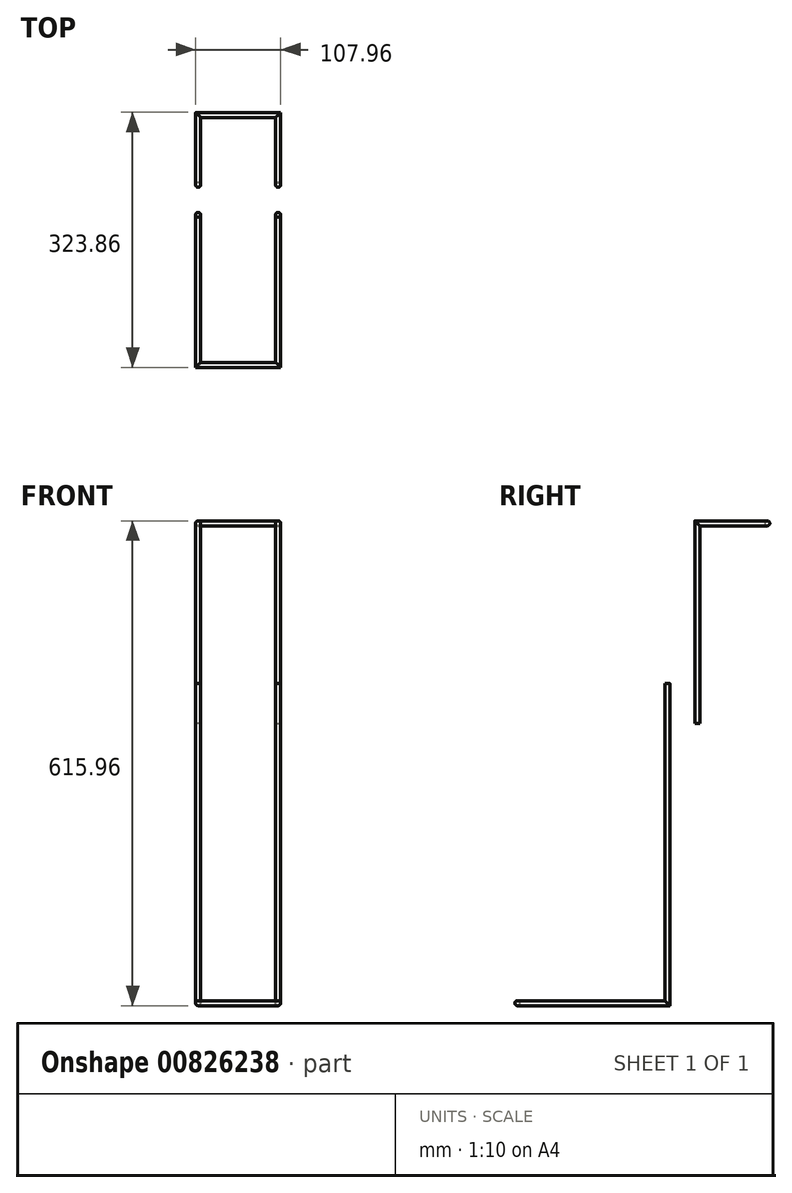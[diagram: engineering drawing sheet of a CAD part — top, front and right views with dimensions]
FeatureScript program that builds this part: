
annotation { "Feature Type Name" : "Feature", "Feature Type Description" : "" }
export const myFeature = defineFeature(function(context is Context, id is Id, definition is map)
    precondition{}
    {
        {
            var Q0;
            Q0=qCreatedBy(makeId("Top.planeOp"),FACE);
            var sketch = newSketch(context, id + "F0", { "sketchPlane" : qUnion([Q0])});
            skPoint(sketch, "E0.0", {"position": v(0, 0) * mm});
            skLineSegment(sketch, "E1", {"start": v(0, 0) * mm, "end": v(0, 88.9) * mm});
            skLineSegment(sketch, "E2", {"start": v(0, 88.9) * mm, "end": v(101.6, 88.9) * mm});
            skLineSegment(sketch, "E3", {"start": v(101.6, 88.9) * mm, "end": v(101.6, 0) * mm});
            skSolve(sketch);
        }
        {
            var Q0;
            Q0=qCreatedBy(makeId("Front.planeOp"),FACE);
            var sketch = newSketch(context, id + "F1", { "sketchPlane" : qUnion([Q0])});
            skPoint(sketch, "E4.0", {"position": v(101.6, 0) * mm});
            skLineSegment(sketch, "E5", {"start": v(101.6, 0) * mm, "end": v(101.6, -254) * mm});
            skLineSegment(sketch, "E6", {"start": v(0, 0) * mm, "end": v(0, -254) * mm});
            skSolve(sketch);
        }
        {
            var Q0;
            Q0=qCreatedBy(makeId("Top.planeOp"),FACE);
            cPlane(context, id + "F2", {"entities" : qUnion([Q0]), "cplaneType" : CPlaneType.OFFSET, "offset" : 254 * mm, "oppositeDirection" : true, "width" : 152.4 * mm, "height" : 152.4 * mm});
        }
        {
            var Q0;
            Q0=qCreatedBy(id+"F2.planeOp",FACE);
            var sketch = newSketch(context, id + "F3", { "sketchPlane" : qUnion([Q0])});
            skPoint(sketch, "E7.0", {"position": v(0, 0) * mm});
            skCircle(sketch, "E8", {"center": v(0, 0) * mm, "radius": 3.18 * mm});
            skSolve(sketch);
        }
        {
            var Q0;
            Q0=makeQuery(id+"F3.imprint","IMPRINT",FACE,{"disambiguationData":[TD([[makeQuery(id+"F3.imprint","IMPRINT",EDGE,{"derivedFrom":sQuery(id+"F3.wireOp",EDGE,"E8")}),1.0]])]});
            var Q1;
            Q1=sQuery(id+"F1.wireOp",EDGE,"E6");
            var Q2;
            Q2=sQuery(id+"F0.wireOp",EDGE,"E1");
            var Q3;
            Q3=sQuery(id+"F0.wireOp",EDGE,"E2");
            var Q4;
            Q4=sQuery(id+"F0.wireOp",EDGE,"E3");
            var Q5;
            Q5=sQuery(id+"F1.wireOp",EDGE,"E5");
            sweep(context, id + "F4", {"profiles" : qUnion([Q0]), "path" : qUnion([Q1, Q2, Q3, Q4, Q5])});
        }
        {
            var Q0;
            Q0=qCreatedBy(makeId("Top.planeOp"),FACE);
            cPlane(context, id + "F5", {"entities" : qUnion([Q0]), "cplaneType" : CPlaneType.OFFSET, "offset" : 203.2 * mm, "oppositeDirection" : true, "width" : 152.4 * mm, "height" : 152.4 * mm});
        }
        {
            var Q0;
            Q0=qCreatedBy(id+"F5.planeOp",FACE);
            var sketch = newSketch(context, id + "F6", { "sketchPlane" : qUnion([Q0])});
            skPoint(sketch, "E9.0", {"position": v(0, 0) * mm});
            skLineSegment(sketch, "E10", {"start": v(0, 0) * mm, "end": v(101.6, 0) * mm});
            skLineSegment(sketch, "E11", {"start": v(0, 0) * mm, "end": v(0, -19.05) * mm});
            skLineSegment(sketch, "E12", {"start": v(101.6, 0) * mm, "end": v(101.6, -19.05) * mm});
            skCircle(sketch, "E13", {"center": v(0, -19.05) * mm, "radius": 3.18 * mm});
            skCircle(sketch, "E14", {"center": v(101.6, -19.05) * mm, "radius": 3.18 * mm});
            skSolve(sketch);
        }
        {
            var Q0;
            Q0=qCreatedBy(makeId("Front.planeOp"),FACE);
            cPlane(context, id + "F7", {"entities" : qUnion([Q0]), "cplaneType" : CPlaneType.OFFSET, "offset" : 38.1 * mm, "width" : 152.4 * mm, "height" : 152.4 * mm});
        }
        {
            var Q0;
            Q0=qCreatedBy(id+"F7.planeOp",FACE);
            var sketch = newSketch(context, id + "F8", { "sketchPlane" : qUnion([Q0])});
            skPoint(sketch, "E15.0", {"position": v(0, -203.2) * mm});
            skPoint(sketch, "E16.0", {"position": v(101.6, -203.2) * mm});
            skLineSegment(sketch, "E17", {"start": v(0, -203.2) * mm, "end": v(0, -609.6) * mm});
            skLineSegment(sketch, "E18", {"start": v(101.6, -203.2) * mm, "end": v(101.6, -609.6) * mm});
            skSolve(sketch);
        }
        {
            var Q0;
            Q0=qCreatedBy(makeId("Top.planeOp"),FACE);
            cPlane(context, id + "F9", {"entities" : qUnion([Q0]), "cplaneType" : CPlaneType.OFFSET, "offset" : 609.6 * mm, "oppositeDirection" : true, "width" : 152.4 * mm, "height" : 152.4 * mm});
        }
        {
            var Q0;
            Q0=qCreatedBy(id+"F9.planeOp",FACE);
            var sketch = newSketch(context, id + "F10", { "sketchPlane" : qUnion([Q0])});
            skPoint(sketch, "E19.0", {"position": v(0, -38.1) * mm});
            skPoint(sketch, "E20.0", {"position": v(101.6, -38.1) * mm});
            skLineSegment(sketch, "E21", {"start": v(0, -38.1) * mm, "end": v(0, -228.6) * mm});
            skLineSegment(sketch, "E22", {"start": v(101.6, -38.1) * mm, "end": v(101.6, -228.6) * mm});
            skLineSegment(sketch, "E23", {"start": v(0, -228.6) * mm, "end": v(101.6, -228.6) * mm});
            skSolve(sketch);
        }
        {
            var Q0;
            Q0=qCreatedBy(id+"F5.planeOp",FACE);
            cPlane(context, id + "F11", {"entities" : qUnion([Q0]), "cplaneType" : CPlaneType.OFFSET, "offset" : 44.45 * mm, "oppositeDirection" : true, "width" : 152.4 * mm, "height" : 152.4 * mm});
        }
        {
            var Q0;
            Q0=qCreatedBy(id+"F5.planeOp",FACE);
            var sketch = newSketch(context, id + "F12", { "sketchPlane" : qUnion([Q0])});
            skPoint(sketch, "E24.0", {"position": v(0, -38.1) * mm});
            skCircle(sketch, "E25", {"center": v(0, -38.1) * mm, "radius": 3.17 * mm});
            skSolve(sketch);
        }
        {
            var Q0;
            Q0=makeQuery(id+"F12.imprint","IMPRINT",FACE,{"disambiguationData":[TD([[makeQuery(id+"F12.imprint","IMPRINT",EDGE,{"derivedFrom":sQuery(id+"F12.wireOp",EDGE,"E25")}),1.0]])]});
            var Q1;
            Q1=sQuery(id+"F8.wireOp",EDGE,"E17");
            var Q2;
            Q2=sQuery(id+"F10.wireOp",EDGE,"E21");
            var Q3;
            Q3=sQuery(id+"F10.wireOp",EDGE,"E23");
            var Q4;
            Q4=sQuery(id+"F10.wireOp",EDGE,"E22");
            var Q5;
            Q5=sQuery(id+"F8.wireOp",EDGE,"E18");
            sweep(context, id + "F13", {"profiles" : qUnion([Q0]), "path" : qUnion([Q1, Q2, Q3, Q4, Q5])});
        }
        {
            var Q0;
            Q0=qCreatedBy(id+"F11.planeOp",FACE);
            cPlane(context, id + "F14", {"entities" : qUnion([Q0]), "cplaneType" : CPlaneType.OFFSET, "offset" : 12.7 * mm, "width" : 152.4 * mm, "height" : 152.4 * mm});
        }
    });
